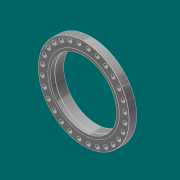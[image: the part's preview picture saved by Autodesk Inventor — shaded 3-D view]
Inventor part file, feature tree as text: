
AUTODESK INVENTOR PART (.ipt)
format: ipt  version: 2017.3 (Build 213256000, 256)  size: 335,360 bytes
history: native  units: in
note: dims shown in document units (in); Inventor stores cm internally (conversion verified against a paired STEP export)
features: sketch x5, extrude x3, chamfer x3, fillet x2, hole x1, pattern_circular x1, revolve x1
ambient origin geometry x8: Origin, YZ Plane, XZ Plane, XY Plane, X Axis, Y Axis, Z Axis, Center Point
bodies: Solid1 (feature_tree)
feature tree (16):
  extrude  "Extrusion1"  Depth=31.0in
  extrude  "Extrusion2"  Depth=3.625in
  extrude  "Extrusion3"  Depth=0.0625in
  hole  "Hole1"  [1 undecoded]
  chamfer  "Chamfer3"  Distance=11.0236in Angle=360.0deg
  pattern_circular  "Circular Pattern1"  [2 undecoded]
  chamfer  "Chamfer2"  Distance=0.4375in
  fillet  "Fillet2"  Radius=0.0312in
  chamfer  "Chamfer4"  Distance=0.0625in Angle=45.0deg
  revolve  "Revolution1"  Angle=90.0deg
  fillet  "Fillet5"  Radius=2.0in
  sketch  "Sketch1"  dims[d0=43.0in d1=31.0in]
  sketch  "Sketch2"  dims[d2=3.625in d3=0.0in d4=33.75in]
  sketch  "Sketch3"  dims[d5=0.0625in d6=0.0in d7=34.75in]
  sketch  "Sketch4"  dims[d8=2.4375in d9=0.0in d13=19.625in]
  sketch  "Sketch6"  dims[d14=0.0442in d15=1.875in d16=0.75in d17=0.375in d18=0.25in d19=0.5635in d20=1.0in d21=0.8108in d22=11.0236in d23=360.0deg d25=0.0625in d26=0.125in d27=0.0687in d29=0.4375in d30=0.0312in d31=0.125in d32=45.0deg d33=0.0625in d34=0.125in d35=45.0deg d49=90.0deg d71=2.0in d72=15.625in d73=0.0312in d94=16.0in d95=0.4375in d96=0.2577in d99=0.5in d100=0.625in d101=0.2893in]
note: 3 required parameter values undecoded (feature->parameter linkage not recoverable at this tier; creation-order binding heuristic only, values carry confidence <= 0.55)
